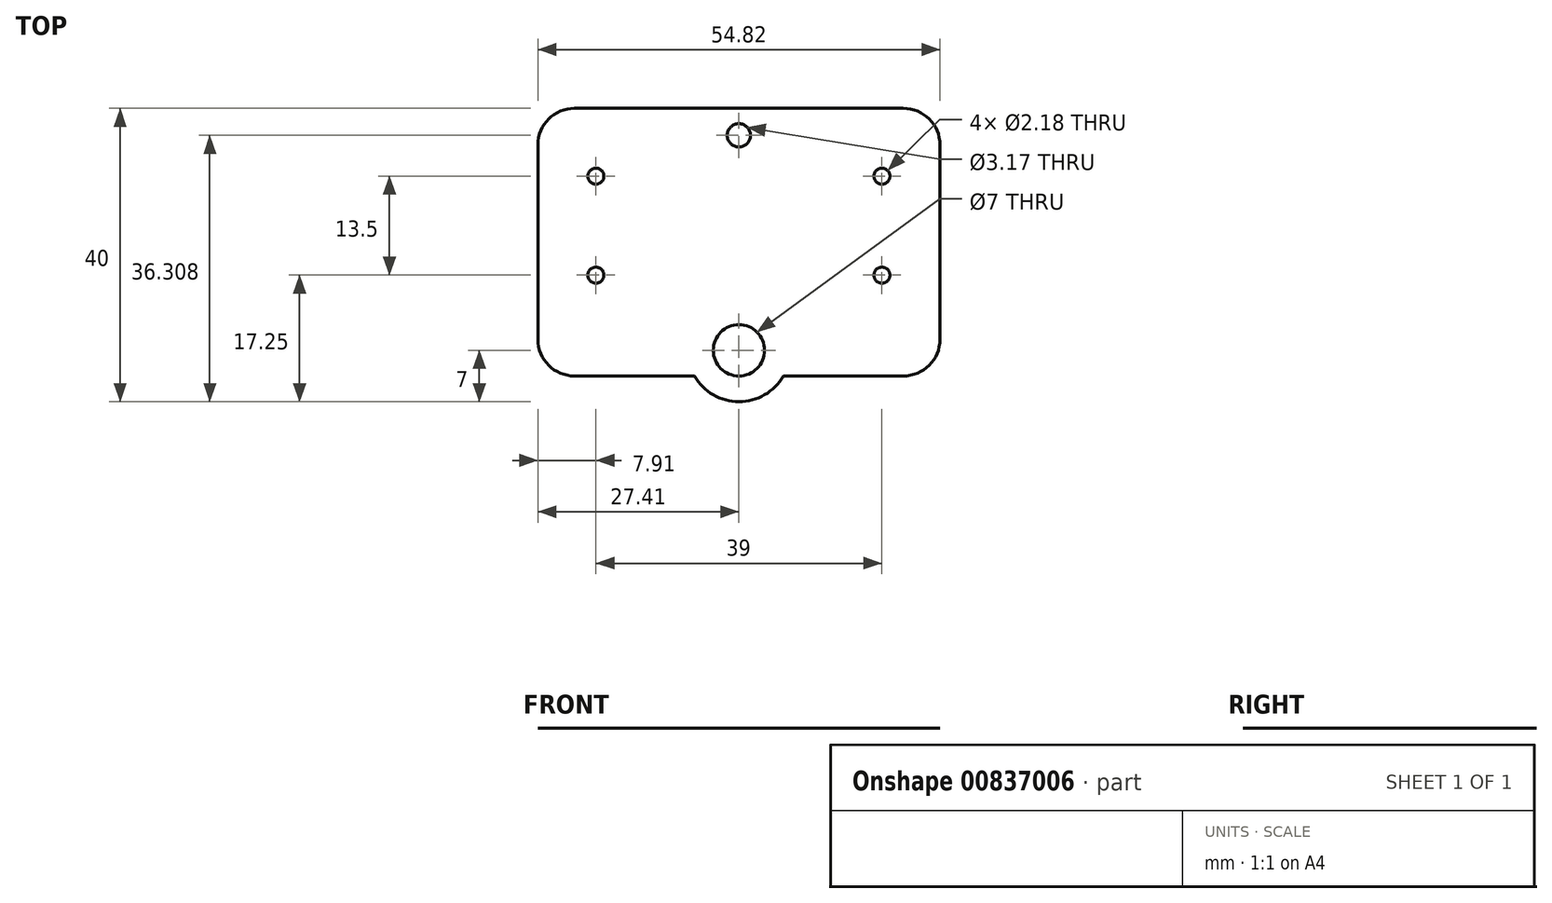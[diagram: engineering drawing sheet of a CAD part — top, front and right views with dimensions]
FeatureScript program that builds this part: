
annotation { "Feature Type Name" : "Feature", "Feature Type Description" : "" }
export const myFeature = defineFeature(function(context is Context, id is Id, definition is map)
    precondition{}
    {
        {
            var Q0;
            Q0=qCreatedBy(makeId("Top.planeOp"),FACE);
            var sketch = newSketch(context, id + "F0", { "sketchPlane" : qUnion([Q0])});
            skLineSegment(sketch, "E0.bottom", {"start": v(22, -9) * mm, "end": v(-22, -9) * mm});
            skLineSegment(sketch, "E0.top", {"start": v(22, 9) * mm, "end": v(-22, 9) * mm});
            skLineSegment(sketch, "E0.left", {"start": v(22, -9) * mm, "end": v(22, 9) * mm});
            skLineSegment(sketch, "E0.right", {"start": v(-22, -9) * mm, "end": v(-22, 9) * mm});
            skPoint(sketch, "E0.middle", {"position": v(0, 0) * mm});
            skLineSegment(sketch, "E1.bottom", {"start": v(-22.41, 16) * mm, "end": v(22.41, 16) * mm});
            skLineSegment(sketch, "E1.top", {"start": v(-22.41, -20.5) * mm, "end": v(22.41, -20.5) * mm});
            skLineSegment(sketch, "E1.left", {"start": v(-27.41, 11) * mm, "end": v(-27.41, -15.5) * mm});
            skLineSegment(sketch, "E1.right", {"start": v(27.41, 11) * mm, "end": v(27.41, -15.5) * mm});
            skPoint(sketch, "E2", {"position": v(0, 16) * mm});
            skLineSegment(sketch, "E3", {"start": v(0, 16) * mm, "end": v(0, 0) * mm});
            skCircle(sketch, "E4", {"center": v(0, 12.3) * mm, "radius": 1.59 * mm});
            skCircle(sketch, "E5", {"center": v(0, -17) * mm, "radius": 3.5 * mm});
            skPoint(sketch, "E6", {"position": v(0, -20.5) * mm});
            skCircle(sketch, "E7", {"center": v(0, -17) * mm, "radius": 7 * mm});
            skLineSegment(sketch, "E8.bottom", {"start": v(19.5, -6.75) * mm, "end": v(-19.5, -6.75) * mm});
            skLineSegment(sketch, "E8.top", {"start": v(19.5, 6.75) * mm, "end": v(-19.5, 6.75) * mm});
            skLineSegment(sketch, "E8.left", {"start": v(19.5, -6.75) * mm, "end": v(19.5, 6.75) * mm});
            skLineSegment(sketch, "E8.right", {"start": v(-19.5, -6.75) * mm, "end": v(-19.5, 6.75) * mm});
            skCircle(sketch, "E9", {"center": v(-19.5, 6.75) * mm, "radius": 1.1 * mm});
            skCircle(sketch, "E10", {"center": v(-19.5, -6.75) * mm, "radius": 1.1 * mm});
            skCircle(sketch, "E11", {"center": v(19.5, 6.75) * mm, "radius": 1.1 * mm});
            skCircle(sketch, "E12", {"center": v(19.5, -6.75) * mm, "radius": 1.1 * mm});
            skPoint(sketch, "E13.visualSharp", {"position": v(-27.41, 16) * mm});
            skArc(sketch, "E13.filletArc", {"start": v(-22.41, 16) * mm, "mid": v(-25.95, 14.54) * mm, "end": v(-27.41, 11) * mm});
            skPoint(sketch, "E14.visualSharp", {"position": v(27.41, 16) * mm});
            skArc(sketch, "E14.filletArc", {"start": v(27.41, 11) * mm, "mid": v(25.95, 14.54) * mm, "end": v(22.41, 16) * mm});
            skPoint(sketch, "E15.visualSharp", {"position": v(27.41, -20.5) * mm});
            skArc(sketch, "E15.filletArc", {"start": v(22.41, -20.5) * mm, "mid": v(25.95, -19.04) * mm, "end": v(27.41, -15.5) * mm});
            skPoint(sketch, "E16.visualSharp", {"position": v(-27.41, -20.5) * mm});
            skArc(sketch, "E16.filletArc", {"start": v(-27.41, -15.5) * mm, "mid": v(-25.95, -19.04) * mm, "end": v(-22.41, -20.5) * mm});
            skSolve(sketch);
        }
        {
            var Q0;
            Q0 = qSketchRegion(id + "F0", true);
            var Q1;
            {var subQ0=sQuery(id+"F0.wireOp",EDGE,"E7");var subQ1=sQuery(id+"F0.wireOp",EDGE,"E0.bottom");var subQ2=makeQuery(id+"F0.imprint","INTERSECT",VERTEX,{"disambiguationData":[OD(0.0)],"derivedFrom":[subQ1,subQ0]});Q1=makeQuery(id+"F0.imprint","IMPRINT",FACE,{"disambiguationData":[TD([[makeQuery(id+"F0.imprint","IMPRINT",EDGE,{"disambiguationData":[TD([[subQ2,-1.0]])],"derivedFrom":subQ1}),-1.0]])]});}
            var Q2;
            {var subQ3=sQuery(id+"F0.wireOp",EDGE,"E0.left");Q2=makeQuery(id+"F0.imprint","IMPRINT",FACE,{"disambiguationData":[TD([[makeQuery(id+"F0.imprint","IMPRINT",EDGE,{"derivedFrom":subQ3}),1.0]])]});}
            var Q3;
            {var subQ7=sQuery(id+"F0.wireOp",EDGE,"E8.top");var subQ8=makeQuery(id+"F0.imprint","IMPRINT",VERTEX,{"derivedFrom":subQ7});Q3=makeQuery(id+"F0.imprint","IMPRINT",FACE,{"disambiguationData":[TD([[makeQuery(id+"F0.imprint","IMPRINT",EDGE,{"disambiguationData":[TD([[subQ8,1.0]])],"derivedFrom":subQ7}),1.0]])]});}
            extrude(context, id + "F1", {"entities" : qUnion([Q0, Q1, Q2, Q3]), "depth" : 1 / 203.2 * mm, "offsetDistance" : 25 * mm});
        }
    });
